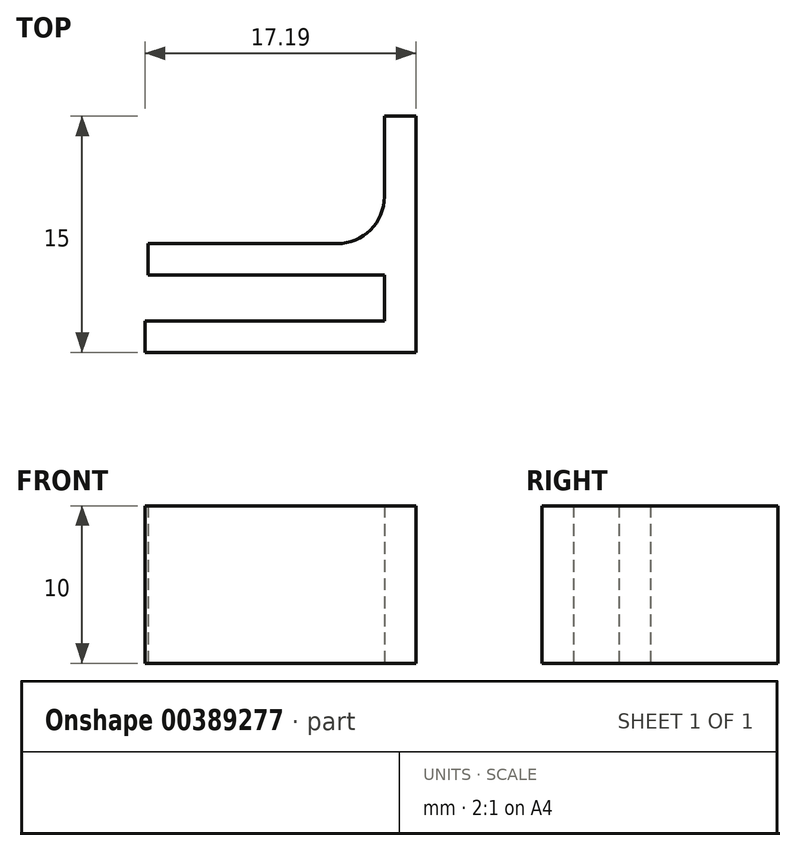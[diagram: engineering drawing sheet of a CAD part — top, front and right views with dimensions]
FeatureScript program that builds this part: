
annotation { "Feature Type Name" : "Feature", "Feature Type Description" : "" }
export const myFeature = defineFeature(function(context is Context, id is Id, definition is map)
    precondition{}
    {
        {
            var Q0;
            Q0=qCreatedBy(makeId("Top.planeOp"), FACE);
            var sketch = newSketch(context, id + "F0", { "sketchPlane" : qUnion([Q0])});
            skLineSegment(sketch, "E0", {"start": v(-15.2, 0) * mm, "end": v(0, 0) * mm});
            skLineSegment(sketch, "E1", {"start": v(0, 0) * mm, "end": v(0, 2.9) * mm});
            skLineSegment(sketch, "E2", {"start": v(0, 2.9) * mm, "end": v(-15, 2.9) * mm});
            skLineSegment(sketch, "E3", {"start": v(-15, 2.9) * mm, "end": v(-15, 4.9) * mm});
            skLineSegment(sketch, "E4", {"start": v(-15, 4.9) * mm, "end": v(-3, 4.9) * mm});
            skLineSegment(sketch, "E5", {"start": v(0, 4.9) * mm, "end": v(0, 0) * mm});
            skLineSegment(sketch, "E6", {"start": v(-15.2, 0) * mm, "end": v(-15.2, -2) * mm});
            skLineSegment(sketch, "E7", {"start": v(-15.2, -2) * mm, "end": v(0, -2) * mm});
            skLineSegment(sketch, "E8", {"start": v(0, -2) * mm, "end": v(0, 0) * mm});
            skLineSegment(sketch, "E9", {"start": v(0, -2) * mm, "end": v(2, -2) * mm});
            skLineSegment(sketch, "E10", {"start": v(2, -2) * mm, "end": v(2, 13) * mm});
            skLineSegment(sketch, "E11", {"start": v(2, 13) * mm, "end": v(0, 13) * mm});
            skLineSegment(sketch, "E12", {"start": v(0, 13) * mm, "end": v(0, 7.9) * mm});
            skPoint(sketch, "E13.visualSharp", {"position": v(0, 4.9) * mm});
            skArc(sketch, "E13.filletArc", {"start": v(-3, 4.9) * mm, "mid": v(-0.88, 5.78) * mm, "end": v(0, 7.9) * mm});
            skSolve(sketch);
        }
        {
            var Q0;
            Q0 = qSketchRegion(id + "F0", true);
            extrude(context, id + "F1", {"entities" : qUnion([Q0]), "depth" : 10 * mm, "offsetDistance" : 25 * mm});
        }
    });
